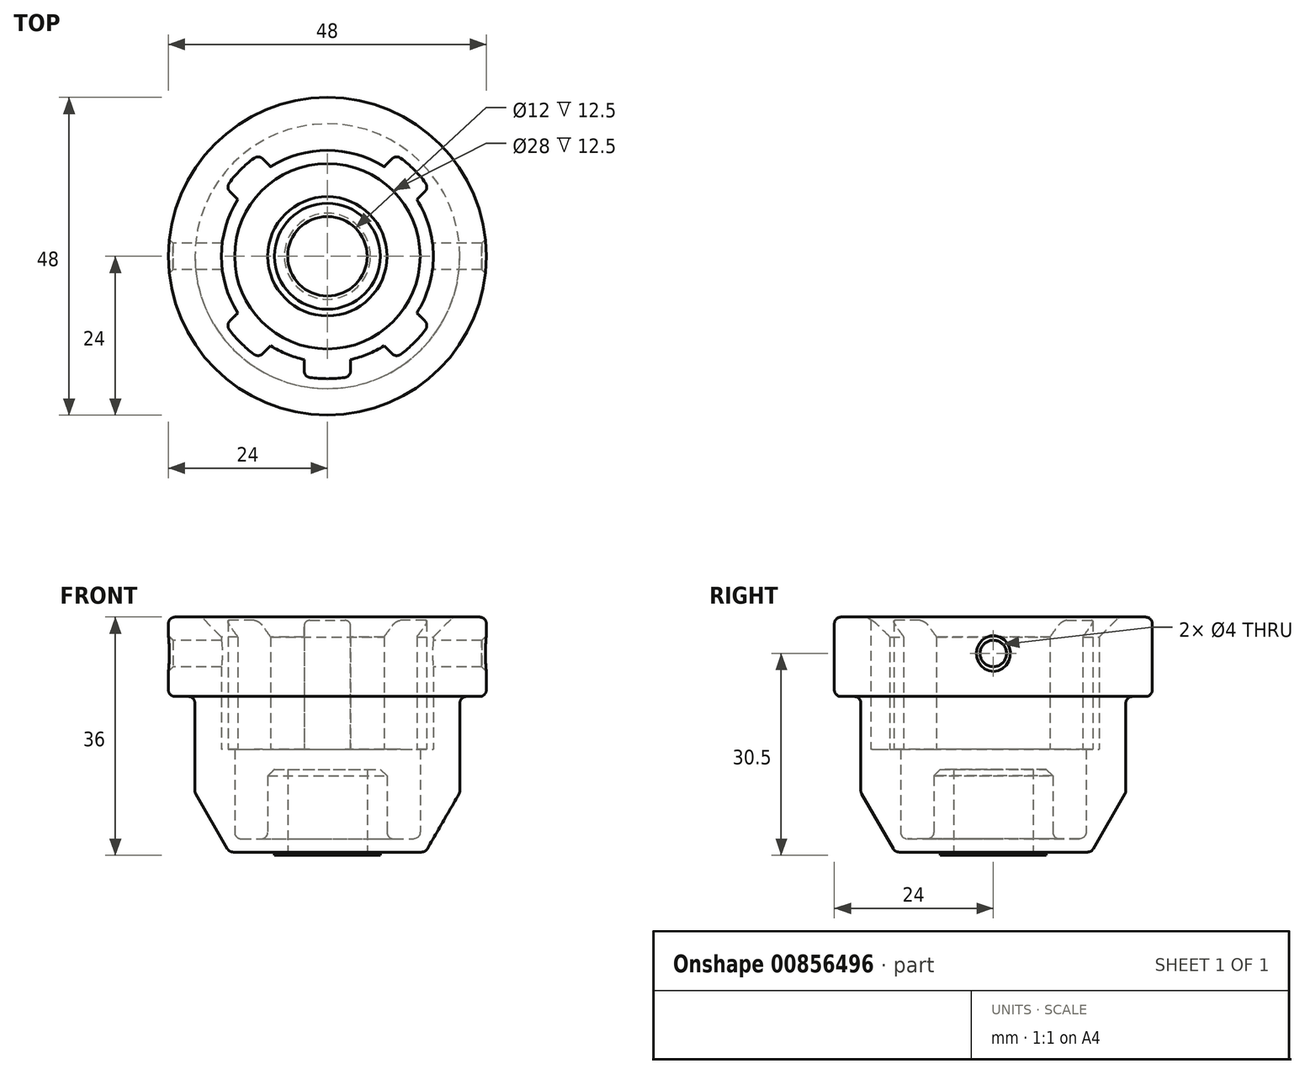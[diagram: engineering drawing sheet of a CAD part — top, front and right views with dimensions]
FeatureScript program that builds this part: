
annotation { "Feature Type Name" : "Feature", "Feature Type Description" : "" }
export const myFeature = defineFeature(function(context is Context, id is Id, definition is map)
    precondition{}
    {
        {
            var Q0;
            Q0=qCreatedBy(makeId("Front.planeOp"),FACE);
            var sketch = newSketch(context, id + "F0", { "sketchPlane" : qUnion([Q0])});
            skLineSegment(sketch, "E0", {"start": v(0, -15) * mm, "end": v(0, 75) * mm, "construction": true});
            skLineSegment(sketch, "E1", {"start": v(-6, 0.5) * mm, "end": v(-6, 13) * mm});
            skLineSegment(sketch, "E2", {"start": v(-6, 13) * mm, "end": v(-8, 13) * mm});
            skLineSegment(sketch, "E3", {"start": v(-9, 12) * mm, "end": v(-8, 13) * mm});
            skLineSegment(sketch, "E4", {"start": v(-9, 12) * mm, "end": v(-9, 2.5) * mm});
            skLineSegment(sketch, "E5", {"start": v(-14, 2.5) * mm, "end": v(-14, 16) * mm});
            skLineSegment(sketch, "E6", {"start": v(-14, 16) * mm, "end": v(-16, 16) * mm});
            skLineSegment(sketch, "E7", {"start": v(-16, 16) * mm, "end": v(-16, 33) * mm});
            skLineSegment(sketch, "E8", {"start": v(-19, 36) * mm, "end": v(-16, 33) * mm});
            skLineSegment(sketch, "E9", {"start": v(-19, 36) * mm, "end": v(-23, 36) * mm});
            skLineSegment(sketch, "E10", {"start": v(-20, 23) * mm, "end": v(-20, 9.5) * mm});
            skLineSegment(sketch, "E11", {"start": v(-14.8, 0.5) * mm, "end": v(-20, 9.5) * mm});
            skLineSegment(sketch, "E12", {"start": v(-14.8, 0.5) * mm, "end": v(-8, 0.5) * mm});
            skLineSegment(sketch, "E13", {"start": v(-8, 0.5) * mm, "end": v(-8, 0) * mm});
            skLineSegment(sketch, "E14", {"start": v(-8, 0) * mm, "end": v(-6.5, 0) * mm});
            skLineSegment(sketch, "E15", {"start": v(-6.5, 0) * mm, "end": v(-6, 0.5) * mm});
            skLineSegment(sketch, "E16", {"start": v(-9, 2.5) * mm, "end": v(-14, 2.5) * mm});
            skLineSegment(sketch, "E17", {"start": v(-21, 24) * mm, "end": v(-23, 24) * mm});
            skLineSegment(sketch, "E18", {"start": v(-24, 25) * mm, "end": v(-24, 35) * mm});
            skArc(sketch, "E19.filletArc", {"start": v(-20, 23) * mm, "mid": v(-20.3, 23.7) * mm, "end": v(-21, 24) * mm});
            skPoint(sketch, "E20.visualSharp", {"position": v(-24, 24) * mm});
            skArc(sketch, "E20.filletArc", {"start": v(-24, 25) * mm, "mid": v(-23.7, 24.3) * mm, "end": v(-23, 24) * mm});
            skPoint(sketch, "E21.visualSharp", {"position": v(-24, 36) * mm});
            skArc(sketch, "E21.filletArc", {"start": v(-23, 36) * mm, "mid": v(-23.7, 35.7) * mm, "end": v(-24, 35) * mm});
            skSolve(sketch);
        }
        {
            var Q0;
            Q0 = qSketchRegion(id + "F0", true);
            var Q1;
            Q1=sQuery(id+"F0.wireOp",EDGE,"E0");
            revolve(context, id + "F1", {"surfaceOperationType" : NewSurfaceOperationType.NEW, "entities" : qUnion([Q0]), "axis" : qUnion([Q1]), "revolveType" : RevolveType.FULL});
        }
        {
            var Q0;
            Q0=makeQuery(id+"F1.opRevolve","SWEPT_FACE",FACE,{"disambiguationData":[OSD([sQuery(id+"F0.wireOp",EDGE,"E6")])]});
            var sketch = newSketch(context, id + "F2", { "sketchPlane" : qUnion([Q0])});
            skCircle(sketch, "E22", {"center": v(0, 0) * mm, "radius": 21.67 * mm, "construction": true});
            skLineSegment(sketch, "E23", {"start": v(15.32, 15.32) * mm, "end": v(-15.32, -15.32) * mm, "construction": true});
            skLineSegment(sketch, "E24", {"start": v(15.32, -15.32) * mm, "end": v(-15.32, 15.32) * mm, "construction": true});
            skLineSegment(sketch, "E25", {"start": v(0, 0) * mm, "end": v(0, -21.67) * mm, "construction": true});
            skArc(sketch, "E26", {"start": v(10.37, -15.32) * mm, "mid": v(13.08, -13.08) * mm, "end": v(15.32, -10.37) * mm});
            skArc(sketch, "E27", {"start": v(12.06, -7.11) * mm, "mid": v(14, 0) * mm, "end": v(12.06, 7.11) * mm});
            skLineSegment(sketch, "E28", {"start": v(3.5, -18.17) * mm, "end": v(3.5, -13.56) * mm});
            skLineSegment(sketch, "E29", {"start": v(-3.5, -18.17) * mm, "end": v(-3.5, -13.56) * mm});
            skLineSegment(sketch, "E30", {"start": v(10.37, -15.32) * mm, "end": v(7.11, -12.06) * mm});
            skLineSegment(sketch, "E31", {"start": v(15.32, -10.37) * mm, "end": v(12.06, -7.11) * mm});
            skArc(sketch, "E32.trimOffspring", {"start": v(3.5, -13.56) * mm, "mid": v(5.36, -12.93) * mm, "end": v(7.11, -12.06) * mm});
            skLineSegment(sketch, "E33", {"start": v(15.32, 10.37) * mm, "end": v(12.06, 7.11) * mm});
            skLineSegment(sketch, "E34", {"start": v(10.37, 15.32) * mm, "end": v(7.11, 12.06) * mm});
            skLineSegment(sketch, "E35", {"start": v(-10.37, 15.32) * mm, "end": v(-7.11, 12.06) * mm});
            skLineSegment(sketch, "E36", {"start": v(-15.32, 10.37) * mm, "end": v(-12.06, 7.11) * mm});
            skLineSegment(sketch, "E37", {"start": v(-10.37, -15.32) * mm, "end": v(-7.11, -12.06) * mm});
            skLineSegment(sketch, "E38", {"start": v(-15.32, -10.37) * mm, "end": v(-12.06, -7.11) * mm});
            skArc(sketch, "E39.trimOffspring", {"start": v(-3.5, -18.17) * mm, "mid": v(0, -18.5) * mm, "end": v(3.5, -18.17) * mm});
            skArc(sketch, "E40.trimOffspring", {"start": v(-7.11, -12.06) * mm, "mid": v(-5.36, -12.93) * mm, "end": v(-3.5, -13.56) * mm});
            skArc(sketch, "E41.trimOffspring", {"start": v(-15.32, -10.37) * mm, "mid": v(-13.08, -13.08) * mm, "end": v(-10.37, -15.32) * mm});
            skArc(sketch, "E42.trimOffspring", {"start": v(-12.06, 7.11) * mm, "mid": v(-14, 0) * mm, "end": v(-12.06, -7.11) * mm});
            skArc(sketch, "E43.trimOffspring", {"start": v(-10.37, 15.32) * mm, "mid": v(-13.08, 13.08) * mm, "end": v(-15.32, 10.37) * mm});
            skArc(sketch, "E44.trimOffspring", {"start": v(7.11, 12.06) * mm, "mid": v(0, 14) * mm, "end": v(-7.11, 12.06) * mm});
            skArc(sketch, "E45.trimOffspring", {"start": v(15.32, 10.37) * mm, "mid": v(13.08, 13.08) * mm, "end": v(10.37, 15.32) * mm});
            skSolve(sketch);
        }
        {
            var Q0;
            Q0 = qSketchRegion(id + "F2", true);
            extrude(context, id + "F3", {"entities" : qUnion([Q0]), "operationType" : NewBodyOperationType.REMOVE, "depth" : 50 * mm, "offsetDistance" : 25 * mm});
        }
        {
            var Q0;
            Q0=makeQuery(id+"F3.boolean.opBoolean","COPY",EDGE,{"derivedFrom":makeQuery(id+"F3.opExtrude","SWEPT_EDGE",EDGE,{"disambiguationData":[OSD([sQuery(id+"F2.wireOp",EDGE,"E35"),sQuery(id+"F2.wireOp",EDGE,"E43.trimOffspring")])]})});
            var Q1;
            Q1=makeQuery(id+"F3.boolean.opBoolean","COPY",EDGE,{"derivedFrom":makeQuery(id+"F3.opExtrude","SWEPT_EDGE",EDGE,{"disambiguationData":[OSD([sQuery(id+"F2.wireOp",EDGE,"E34"),sQuery(id+"F2.wireOp",EDGE,"E45.trimOffspring")])]})});
            var Q2;
            Q2=makeQuery(id+"F3.boolean.opBoolean","COPY",EDGE,{"derivedFrom":makeQuery(id+"F3.opExtrude","SWEPT_EDGE",EDGE,{"disambiguationData":[OSD([sQuery(id+"F2.wireOp",EDGE,"E26"),sQuery(id+"F2.wireOp",EDGE,"E30")])]})});
            var Q3;
            Q3=makeQuery(id+"F3.boolean.opBoolean","COPY",EDGE,{"derivedFrom":makeQuery(id+"F3.opExtrude","SWEPT_EDGE",EDGE,{"disambiguationData":[OSD([sQuery(id+"F2.wireOp",EDGE,"E37"),sQuery(id+"F2.wireOp",EDGE,"E41.trimOffspring")])]})});
            var Q4;
            Q4=makeQuery(id+"F3.boolean.opBoolean","COPY",EDGE,{"derivedFrom":makeQuery(id+"F3.opExtrude","SWEPT_EDGE",EDGE,{"disambiguationData":[OSD([sQuery(id+"F2.wireOp",EDGE,"E28"),sQuery(id+"F2.wireOp",EDGE,"E39.trimOffspring")])]})});
            var Q5;
            Q5=makeQuery(id+"F3.boolean.opBoolean","COPY",EDGE,{"derivedFrom":makeQuery(id+"F3.opExtrude","SWEPT_EDGE",EDGE,{"disambiguationData":[OSD([sQuery(id+"F2.wireOp",EDGE,"E33"),sQuery(id+"F2.wireOp",EDGE,"E45.trimOffspring")])]})});
            var Q6;
            Q6=makeQuery(id+"F3.boolean.opBoolean","COPY",EDGE,{"derivedFrom":makeQuery(id+"F3.opExtrude","SWEPT_EDGE",EDGE,{"disambiguationData":[OSD([sQuery(id+"F2.wireOp",EDGE,"E26"),sQuery(id+"F2.wireOp",EDGE,"E31")])]})});
            var Q7;
            Q7=makeQuery(id+"F3.boolean.opBoolean","COPY",EDGE,{"derivedFrom":makeQuery(id+"F3.opExtrude","SWEPT_EDGE",EDGE,{"disambiguationData":[OSD([sQuery(id+"F2.wireOp",EDGE,"E36"),sQuery(id+"F2.wireOp",EDGE,"E43.trimOffspring")])]})});
            var Q8;
            Q8=makeQuery(id+"F3.boolean.opBoolean","COPY",EDGE,{"derivedFrom":makeQuery(id+"F3.opExtrude","SWEPT_EDGE",EDGE,{"disambiguationData":[OSD([sQuery(id+"F2.wireOp",EDGE,"E29"),sQuery(id+"F2.wireOp",EDGE,"E39.trimOffspring")])]})});
            var Q9;
            Q9=makeQuery(id+"F3.boolean.opBoolean","COPY",EDGE,{"derivedFrom":makeQuery(id+"F3.opExtrude","SWEPT_EDGE",EDGE,{"disambiguationData":[OSD([sQuery(id+"F2.wireOp",EDGE,"E38"),sQuery(id+"F2.wireOp",EDGE,"E41.trimOffspring")])]})});
            fillet(context, id + "F4", {"entities" : qUnion([Q0, Q1, Q2, Q3, Q4, Q5, Q6, Q7, Q8, Q9]), "radius" : 1 * mm, "tangentPropagation" : true, "allowEdgeOverflow" : false});
        }
        {
            var Q0;
            Q0=qCreatedBy(makeId("Front.planeOp"),FACE);
            var sketch = newSketch(context, id + "F5", { "sketchPlane" : qUnion([Q0])});
            skLineSegment(sketch, "E46.bottom", {"start": v(-24, 30.5) * mm, "end": v(24, 30.5) * mm});
            skLineSegment(sketch, "E46.top", {"start": v(-23.3, 28.5) * mm, "end": v(23.3, 28.5) * mm});
            skLineSegment(sketch, "E46.left", {"start": v(-24, 30.5) * mm, "end": v(-24, 27.8) * mm});
            skLineSegment(sketch, "E46.right", {"start": v(24, 30.5) * mm, "end": v(24, 27.8) * mm});
            skLineSegment(sketch, "E47", {"start": v(34, 30.5) * mm, "end": v(-34, 30.5) * mm, "construction": true});
            skLineSegment(sketch, "E48", {"start": v(-23.3, 28.5) * mm, "end": v(-24, 27.8) * mm});
            skLineSegment(sketch, "E49", {"start": v(23.3, 28.5) * mm, "end": v(24, 27.8) * mm});
            skSolve(sketch);
        }
        {
            var Q0;
            Q0 = qSketchRegion(id + "F5", true);
            var Q1;
            Q1=sQuery(id+"F5.wireOp",EDGE,"E47");
            revolve(context, id + "F6", {"operationType" : NewBodyOperationType.REMOVE, "surfaceOperationType" : NewSurfaceOperationType.NEW, "entities" : qUnion([Q0]), "axis" : qUnion([Q1]), "revolveType" : RevolveType.FULL, "oppositeDirection" : true});
        }
        {
            var Q0;
            Q0=makeQuery(id+"F1.opRevolve","SWEPT_EDGE",EDGE,{"disambiguationData":[OSD([sQuery(id+"F0.wireOp",EDGE,"E5"),sQuery(id+"F0.wireOp",EDGE,"E16")])]});
            var Q1;
            Q1=makeQuery(id+"F1.opRevolve","SWEPT_EDGE",EDGE,{"disambiguationData":[OSD([sQuery(id+"F0.wireOp",EDGE,"E4"),sQuery(id+"F0.wireOp",EDGE,"E16")])]});
            fillet(context, id + "F7", {"entities" : qUnion([Q0, Q1]), "radius" : 1 * mm, "tangentPropagation" : true, "allowEdgeOverflow" : false});
        }
        {
            var Q0;
            Q0=makeQuery(id+"F1.opRevolve","SWEPT_EDGE",EDGE,{"disambiguationData":[OSD([sQuery(id+"F0.wireOp",EDGE,"E10"),sQuery(id+"F0.wireOp",EDGE,"E11")])]});
            var Q1;
            Q1=makeQuery(id+"F1.opRevolve","SWEPT_EDGE",EDGE,{"disambiguationData":[OSD([sQuery(id+"F0.wireOp",EDGE,"E11"),sQuery(id+"F0.wireOp",EDGE,"E12")])]});
            fillet(context, id + "F8", {"entities" : qUnion([Q0, Q1]), "radius" : 1 * mm, "tangentPropagation" : true, "allowEdgeOverflow" : false});
        }
        {
            var Q0;
            Q0=makeQuery(id+"F1.opRevolve","SWEPT_EDGE",EDGE,{"disambiguationData":[OSD([sQuery(id+"F0.wireOp",EDGE,"E9"),sQuery(id+"F0.wireOp",EDGE,"E10")])]});
            fillet(context, id + "F9", {"entities" : qUnion([Q0]), "radius" : .5 * mm, "tangentPropagation" : true, "allowEdgeOverflow" : false});
        }
    });
